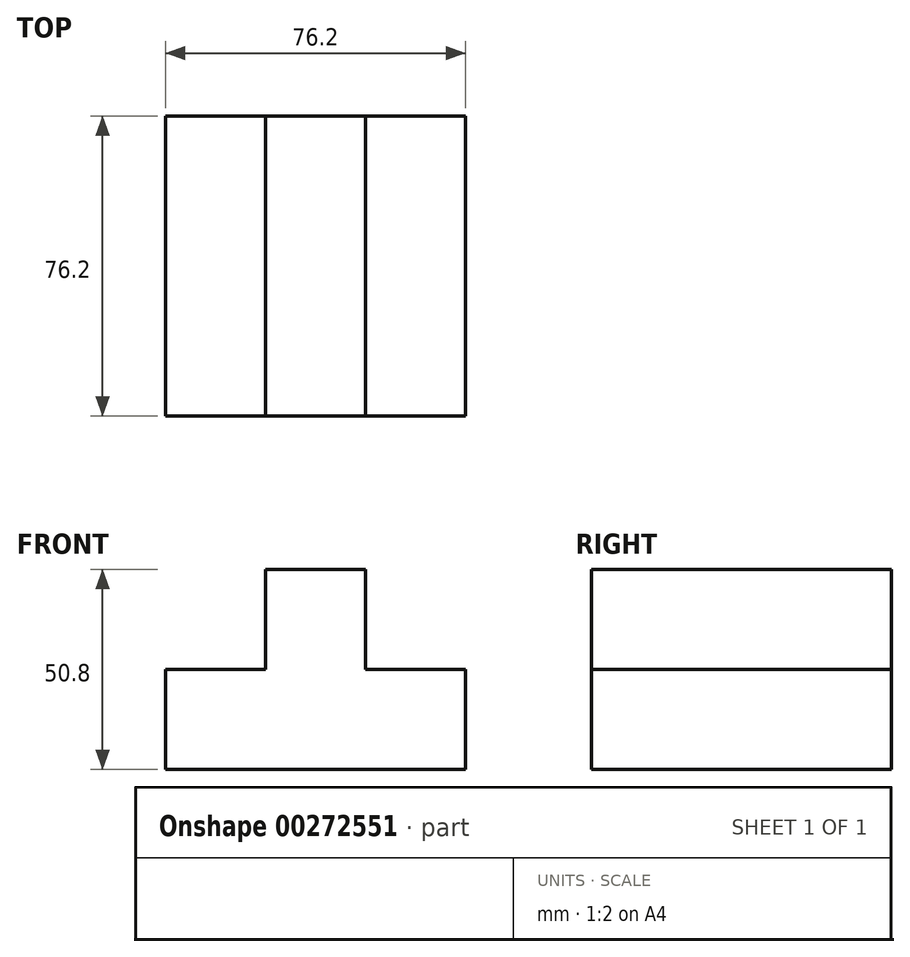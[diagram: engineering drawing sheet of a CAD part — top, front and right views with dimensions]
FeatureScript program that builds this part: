
annotation { "Feature Type Name" : "Feature", "Feature Type Description" : "" }
export const myFeature = defineFeature(function(context is Context, id is Id, definition is map)
    precondition{}
    {
        {
            var Q0;
            Q0=qCreatedBy(makeId("Front.planeOp"),FACE);
            var sketch = newSketch(context, id + "F0", { "sketchPlane" : qUnion([Q0])});
            skLineSegment(sketch, "E0", {"start": v(0, 0) * mm, "end": v(76.2, 0) * mm});
            skLineSegment(sketch, "E1", {"start": v(76.2, 0) * mm, "end": v(76.2, 25.4) * mm});
            skLineSegment(sketch, "E2", {"start": v(76.2, 25.4) * mm, "end": v(50.8, 25.4) * mm});
            skLineSegment(sketch, "E3", {"start": v(50.8, 25.4) * mm, "end": v(50.8, 50.8) * mm});
            skLineSegment(sketch, "E4", {"start": v(50.8, 50.8) * mm, "end": v(25.4, 50.8) * mm});
            skLineSegment(sketch, "E5", {"start": v(25.4, 50.8) * mm, "end": v(25.4, 25.4) * mm});
            skLineSegment(sketch, "E6", {"start": v(25.4, 25.4) * mm, "end": v(0, 25.4) * mm});
            skLineSegment(sketch, "E7", {"start": v(0, 25.4) * mm, "end": v(0, 0) * mm});
            skSolve(sketch);
        }
        {
            var Q0;
            Q0 = qSketchRegion(id + "F0", true);
            extrude(context, id + "F1", {"entities" : qUnion([Q0]), "depth" : 76.2 * mm});
        }
    });
